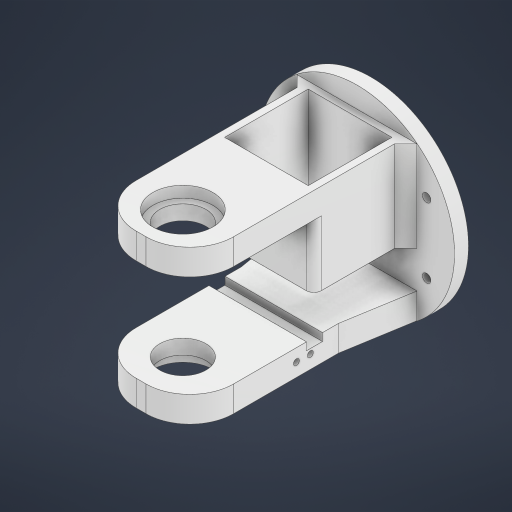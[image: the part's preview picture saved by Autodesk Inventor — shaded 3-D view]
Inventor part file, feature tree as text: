
AUTODESK INVENTOR PART (.ipt)
format: ipt  version: 2024 (Build 280153000, 153)  size: 784,384 bytes
history: native  units: mm
features: extrude x10, sketch x10, other x6, plane x3, fillet x2, chamfer x2, reference x2, move_body x2, direct_edit x1, projected_geometry x1
ambient origin geometry x8: Origin, YZ Plane, XZ Plane, XY Plane, X Axis, Y Axis, Z Axis, Center Point
bodies: Solid1 (feature_tree)
feature tree (39):
  extrude  "Extrusion1"  Depth=10.0mm TaperAngle=0.0deg
  extrude  "Extrusion2"  Depth=35.0mm
  extrude  "Extrusion4"  Depth=70.0mm
  extrude  "Extrusion3"  Depth=155.0mm TaperAngle=0.0deg
  extrude  "Extrusion5"  Depth=60.0mm
  plane  "Work Plane2"
  extrude  "Extrusion6"  Depth=60.0mm TaperAngle=0.0deg
  plane  "Work Plane1"
  other  "tolerance base-arm"
  fillet  "Fillet1"  Radius=45.0mm
  extrude  "Extrusion7"  Depth=30.0mm
  fillet  "Fillet2"  [1 undecoded]
  plane  "Work Plane4"
  extrude  "Extrusion8"  Depth=8.0mm TaperAngle=0.0deg
  chamfer  "Chamfer4"  Distance=27.0mm
  chamfer  "Chamfer5"  Distance=25.0mm
  direct_edit  "Direct Edit2"
  extrude  "Extrusion9"  Depth=3.0mm
  extrude  "Extrusion10"  Depth=50.0mm
  sketch  "Sketch1"  dims[d0=140.0mm d1=10.0mm d2=0.0mm]
  sketch  "Sketch2"  dims[d3=35.0mm d4=35.0mm]
  sketch  "Sketch3"  dims[d5=20.0mm d6=70.0mm]
  sketch  "Sketch4"  dims[d7=35.0mm d8=155.0mm d9=0.0mm]
  sketch  "Sketch5"  dims[d10=60.0mm d11=60.0mm]
  sketch  "Sketch6"  dims[d12=5.0mm d13=60.0mm d14=0.0mm d19=45.0mm d20=0.0mm]
  sketch  "Sketch7"  dims[d28=35.0mm d29=30.0mm d30=0.0mm d31=0.0mm]
  sketch  "Sketch8"  dims[d35=8.0mm d36=8.0mm d37=0.0mm]
  projected_geometry  "Projected Loop1"
  sketch  "Sketch10"  dims[d38=-1.0mm]
  reference  "Reference4"
  sketch  "Sketch11"  dims[d39=31.5mm d40=27.0mm d41=25.0mm d42=25.0mm d43=50.0mm d44=50.0mm d45=15.0mm d46=15.0mm d47=25.0mm d48=25.0mm d49=50.0mm d50=50.0mm d51=6.0mm d52=0.0mm d53=0.0mm d54=5.5mm d55=10.0mm d56=4.2mm d57=9.5mm d58=45.0mm d59=0.0mm d60=0.0mm d61=8.0mm d62=48.25mm d63=45.0deg d64=8.0mm d65=48.25mm d66=45.0deg d67=0.0mm d68=0.0mm d69=-0.5mm d70=0.0mm d71=0.0mm d72=-0.5mm d73=38.0mm d74=43.0mm d75=8.0mm d76=0.0mm d77=3.0mm d78=3.0mm d79=0.75mm d80=0.75mm d81=0.0mm d82=0.0mm d83=2.0mm d84=3.0mm]
  reference  "Reference5"
  other  "Size1"
  move_body  "Move1"
  move_body  "Move2"
  other  "<userpath>\Documents\Inventor\robot arm\arms\arms.iam"
  other  "arms.iam"
  other  "stepper motor large:1"
  other  "base-tensioner-head:1"
note: 1 required parameter value undecoded (feature->parameter linkage not recoverable at this tier; creation-order binding heuristic only, values carry confidence <= 0.55)
